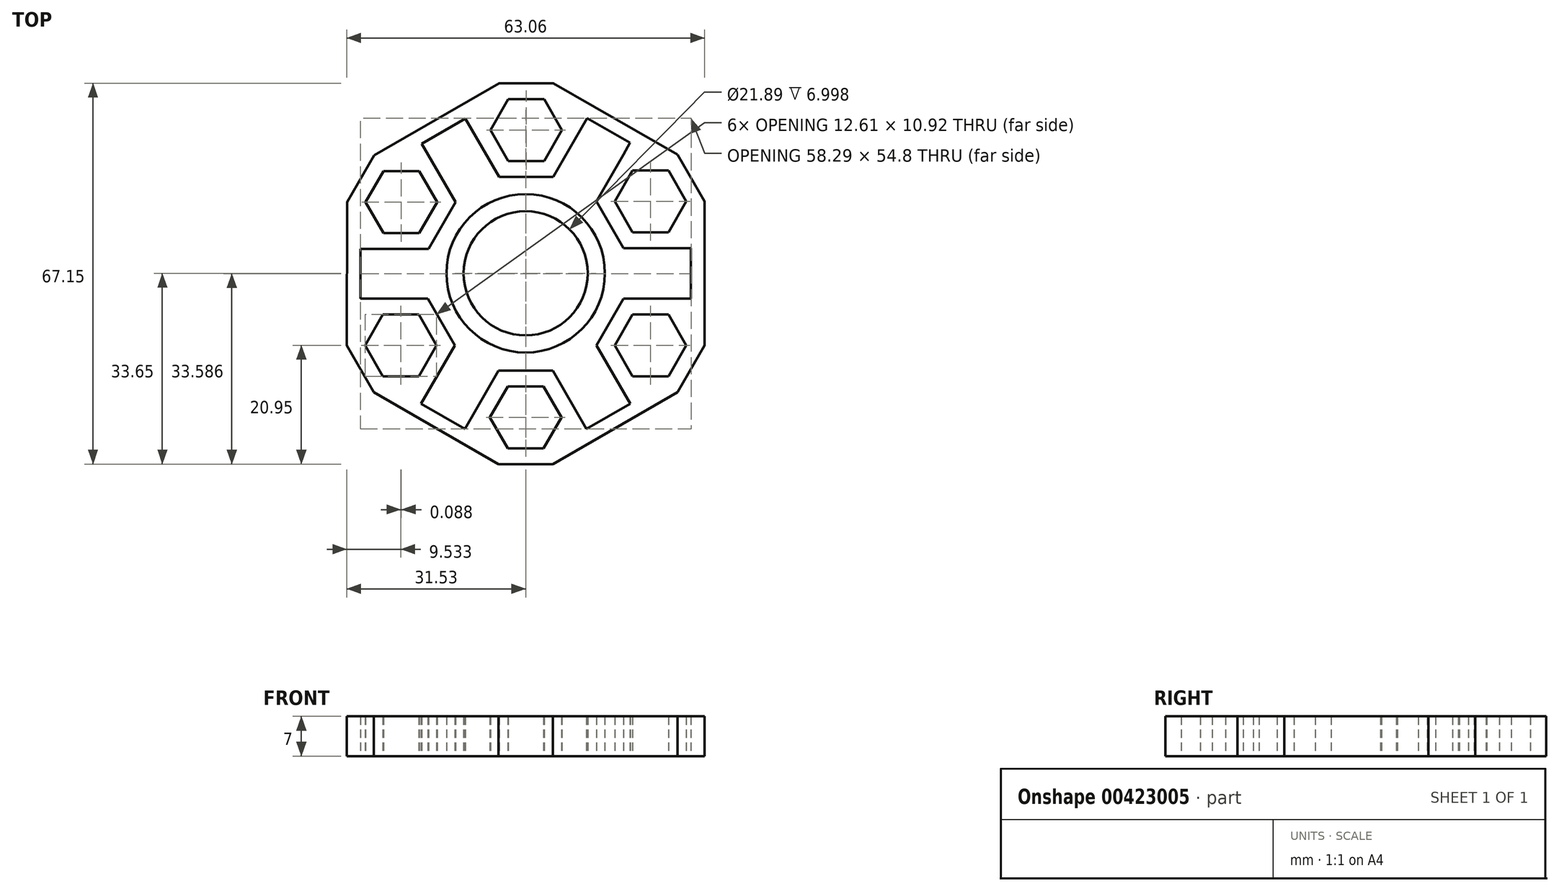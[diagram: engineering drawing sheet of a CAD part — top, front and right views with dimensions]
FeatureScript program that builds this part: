
annotation { "Feature Type Name" : "Feature", "Feature Type Description" : "" }
export const myFeature = defineFeature(function(context is Context, id is Id, definition is map)
    precondition{}
    {
        {
            var Q0;
            Q0=qCreatedBy(makeId("Top.planeOp"),FACE);
            var sketch = newSketch(context, id + "F0", { "sketchPlane" : qUnion([Q0])});
            skCircle(sketch, "E0", {"center": v(0, 0) * mm, "radius": 10.95 * mm});
            skCircle(sketch, "E1.cCircle", {"center": v(0, 0) * mm, "radius": 14.29 * mm, "construction": true});
            skPoint(sketch, "E1.0.midPoint", {"position": v(0, 14.29) * mm});
            skPoint(sketch, "E2.endSnap0", {"position": v(0, -12.7) * mm});
            skCircle(sketch, "E3.cCircle", {"center": v(0.09, 25.25) * mm, "radius": 5.46 * mm, "construction": true});
            skLineSegment(sketch, "E3.0", {"start": v(3.24, 19.79) * mm, "end": v(-3.06, 19.79) * mm});
            skLineSegment(sketch, "E3.1", {"start": v(-3.06, 19.79) * mm, "end": v(-6.22, 25.25) * mm});
            skLineSegment(sketch, "E3.2", {"start": v(-6.22, 25.25) * mm, "end": v(-3.06, 30.7) * mm});
            skLineSegment(sketch, "E3.3", {"start": v(-3.06, 30.7) * mm, "end": v(3.24, 30.7) * mm});
            skLineSegment(sketch, "E3.4", {"start": v(3.24, 30.7) * mm, "end": v(6.4, 25.25) * mm});
            skLineSegment(sketch, "E3.5", {"start": v(6.4, 25.25) * mm, "end": v(3.24, 19.79) * mm});
            skPoint(sketch, "E3.0.midPoint", {"position": v(0.09, 19.79) * mm});
            skCircle(sketch, "E4.cCircle", {"center": v(22, 12.7) * mm, "radius": 5.46 * mm, "construction": true});
            skLineSegment(sketch, "E4.0", {"start": v(18.84, 7.24) * mm, "end": v(15.7, 12.7) * mm});
            skLineSegment(sketch, "E4.1", {"start": v(15.7, 12.7) * mm, "end": v(18.84, 18.16) * mm});
            skLineSegment(sketch, "E4.2", {"start": v(18.84, 18.16) * mm, "end": v(25.15, 18.16) * mm});
            skLineSegment(sketch, "E4.3", {"start": v(25.15, 18.16) * mm, "end": v(28.3, 12.7) * mm});
            skLineSegment(sketch, "E4.4", {"start": v(28.3, 12.7) * mm, "end": v(25.15, 7.24) * mm});
            skLineSegment(sketch, "E4.5", {"start": v(25.15, 7.24) * mm, "end": v(18.84, 7.24) * mm});
            skPoint(sketch, "E4.0.midPoint", {"position": v(17.27, 9.97) * mm});
            skCircle(sketch, "E5.cCircle", {"center": v(22, -12.7) * mm, "radius": 5.46 * mm, "construction": true});
            skLineSegment(sketch, "E5.0", {"start": v(15.7, -12.7) * mm, "end": v(18.84, -7.24) * mm});
            skLineSegment(sketch, "E5.1", {"start": v(18.84, -7.24) * mm, "end": v(25.15, -7.24) * mm});
            skLineSegment(sketch, "E5.2", {"start": v(25.15, -7.24) * mm, "end": v(28.3, -12.7) * mm});
            skLineSegment(sketch, "E5.3", {"start": v(28.3, -12.7) * mm, "end": v(25.15, -18.16) * mm});
            skLineSegment(sketch, "E5.4", {"start": v(25.15, -18.16) * mm, "end": v(18.84, -18.16) * mm});
            skLineSegment(sketch, "E5.5", {"start": v(18.84, -18.16) * mm, "end": v(15.7, -12.7) * mm});
            skPoint(sketch, "E5.0.midPoint", {"position": v(17.27, -9.97) * mm});
            skCircle(sketch, "E6.cCircle", {"center": v(0, -25.4) * mm, "radius": 5.46 * mm, "construction": true});
            skLineSegment(sketch, "E6.0", {"start": v(-3.15, -19.94) * mm, "end": v(3.15, -19.94) * mm});
            skLineSegment(sketch, "E6.1", {"start": v(3.15, -19.94) * mm, "end": v(6.3, -25.4) * mm});
            skLineSegment(sketch, "E6.2", {"start": v(6.3, -25.4) * mm, "end": v(3.15, -30.86) * mm});
            skLineSegment(sketch, "E6.3", {"start": v(3.15, -30.86) * mm, "end": v(-3.15, -30.86) * mm});
            skLineSegment(sketch, "E6.4", {"start": v(-3.15, -30.86) * mm, "end": v(-6.3, -25.4) * mm});
            skLineSegment(sketch, "E6.5", {"start": v(-6.3, -25.4) * mm, "end": v(-3.15, -19.94) * mm});
            skPoint(sketch, "E6.0.midPoint", {"position": v(0, -19.94) * mm});
            skCircle(sketch, "E7.cCircle", {"center": v(-22, -12.7) * mm, "radius": 5.46 * mm, "construction": true});
            skLineSegment(sketch, "E7.0", {"start": v(-18.84, -7.24) * mm, "end": v(-15.7, -12.7) * mm});
            skLineSegment(sketch, "E7.1", {"start": v(-15.7, -12.7) * mm, "end": v(-18.84, -18.16) * mm});
            skLineSegment(sketch, "E7.2", {"start": v(-18.84, -18.16) * mm, "end": v(-25.15, -18.16) * mm});
            skLineSegment(sketch, "E7.3", {"start": v(-25.15, -18.16) * mm, "end": v(-28.3, -12.7) * mm});
            skLineSegment(sketch, "E7.4", {"start": v(-28.3, -12.7) * mm, "end": v(-25.15, -7.24) * mm});
            skLineSegment(sketch, "E7.5", {"start": v(-25.15, -7.24) * mm, "end": v(-18.84, -7.24) * mm});
            skPoint(sketch, "E7.0.midPoint", {"position": v(-17.27, -9.97) * mm});
            skCircle(sketch, "E8.cCircle", {"center": v(-21.9, 12.55) * mm, "radius": 5.46 * mm, "construction": true});
            skLineSegment(sketch, "E8.0", {"start": v(-15.6, 12.55) * mm, "end": v(-18.76, 7.09) * mm});
            skLineSegment(sketch, "E8.1", {"start": v(-18.76, 7.09) * mm, "end": v(-25.06, 7.09) * mm});
            skLineSegment(sketch, "E8.2", {"start": v(-25.06, 7.09) * mm, "end": v(-28.21, 12.55) * mm});
            skLineSegment(sketch, "E8.3", {"start": v(-28.21, 12.55) * mm, "end": v(-25.06, 18) * mm});
            skLineSegment(sketch, "E8.4", {"start": v(-25.06, 18) * mm, "end": v(-18.76, 18) * mm});
            skLineSegment(sketch, "E8.5", {"start": v(-18.76, 18) * mm, "end": v(-15.6, 12.55) * mm});
            skPoint(sketch, "E8.0.midPoint", {"position": v(-17.18, 9.82) * mm});
            skCircle(sketch, "E9.cCircle", {"center": v(-21.9, 12.55) * mm, "radius": 8.26 * mm, "construction": true});
            skLineSegment(sketch, "E9.0", {"start": v(-12.38, 12.55) * mm, "end": v(-17.14, 4.3) * mm});
            skLineSegment(sketch, "E9.1", {"start": v(-17.14, 4.3) * mm, "end": v(-26.67, 4.3) * mm});
            skLineSegment(sketch, "E9.2", {"start": v(-26.67, 4.3) * mm, "end": v(-31.44, 12.55) * mm});
            skLineSegment(sketch, "E9.3", {"start": v(-31.44, 12.55) * mm, "end": v(-26.67, 20.8) * mm});
            skLineSegment(sketch, "E9.4", {"start": v(-26.67, 20.8) * mm, "end": v(-17.14, 20.8) * mm});
            skLineSegment(sketch, "E9.5", {"start": v(-17.14, 20.8) * mm, "end": v(-12.38, 12.55) * mm});
            skPoint(sketch, "E9.0.midPoint", {"position": v(-14.76, 8.42) * mm});
            skCircle(sketch, "E10.cCircle", {"center": v(0.09, 25.25) * mm, "radius": 8.26 * mm, "construction": true});
            skLineSegment(sketch, "E10.0", {"start": v(4.85, 17) * mm, "end": v(-4.68, 17) * mm});
            skLineSegment(sketch, "E10.1", {"start": v(-4.68, 17) * mm, "end": v(-9.44, 25.25) * mm});
            skLineSegment(sketch, "E10.2", {"start": v(-9.44, 25.25) * mm, "end": v(-4.68, 33.5) * mm});
            skLineSegment(sketch, "E10.3", {"start": v(-4.68, 33.5) * mm, "end": v(4.85, 33.5) * mm});
            skLineSegment(sketch, "E10.4", {"start": v(4.85, 33.5) * mm, "end": v(9.62, 25.25) * mm});
            skLineSegment(sketch, "E10.5", {"start": v(9.62, 25.25) * mm, "end": v(4.85, 17) * mm});
            skPoint(sketch, "E10.0.midPoint", {"position": v(0.09, 17) * mm});
            skCircle(sketch, "E11.cCircle", {"center": v(22, 12.7) * mm, "radius": 8.26 * mm, "construction": true});
            skLineSegment(sketch, "E11.0", {"start": v(17.23, 4.45) * mm, "end": v(12.46, 12.7) * mm});
            skLineSegment(sketch, "E11.1", {"start": v(12.46, 12.7) * mm, "end": v(17.23, 20.96) * mm});
            skLineSegment(sketch, "E11.2", {"start": v(17.23, 20.96) * mm, "end": v(26.76, 20.96) * mm});
            skLineSegment(sketch, "E11.3", {"start": v(26.76, 20.96) * mm, "end": v(31.53, 12.7) * mm});
            skLineSegment(sketch, "E11.4", {"start": v(31.53, 12.7) * mm, "end": v(26.76, 4.45) * mm});
            skLineSegment(sketch, "E11.5", {"start": v(26.76, 4.45) * mm, "end": v(17.23, 4.45) * mm});
            skPoint(sketch, "E11.0.midPoint", {"position": v(14.85, 8.57) * mm});
            skCircle(sketch, "E12.cCircle", {"center": v(22, -12.7) * mm, "radius": 8.26 * mm, "construction": true});
            skLineSegment(sketch, "E12.0", {"start": v(12.46, -12.7) * mm, "end": v(17.23, -4.44) * mm});
            skLineSegment(sketch, "E12.1", {"start": v(17.23, -4.45) * mm, "end": v(26.76, -4.44) * mm});
            skLineSegment(sketch, "E12.2", {"start": v(26.76, -4.44) * mm, "end": v(31.53, -12.7) * mm});
            skLineSegment(sketch, "E12.3", {"start": v(31.53, -12.7) * mm, "end": v(26.76, -20.96) * mm});
            skLineSegment(sketch, "E12.4", {"start": v(26.76, -20.96) * mm, "end": v(17.23, -20.96) * mm});
            skLineSegment(sketch, "E12.5", {"start": v(17.23, -20.96) * mm, "end": v(12.46, -12.7) * mm});
            skPoint(sketch, "E12.0.midPoint", {"position": v(14.85, -8.57) * mm});
            skCircle(sketch, "E13.cCircle", {"center": v(0, -25.4) * mm, "radius": 8.26 * mm, "construction": true});
            skLineSegment(sketch, "E13.0", {"start": v(-4.77, -17.14) * mm, "end": v(4.77, -17.14) * mm});
            skLineSegment(sketch, "E13.1", {"start": v(4.77, -17.15) * mm, "end": v(9.53, -25.4) * mm});
            skLineSegment(sketch, "E13.2", {"start": v(9.53, -25.4) * mm, "end": v(4.77, -33.65) * mm});
            skLineSegment(sketch, "E13.3", {"start": v(4.77, -33.65) * mm, "end": v(-4.77, -33.66) * mm});
            skLineSegment(sketch, "E13.4", {"start": v(-4.77, -33.66) * mm, "end": v(-9.53, -25.4) * mm});
            skLineSegment(sketch, "E13.5", {"start": v(-9.53, -25.4) * mm, "end": v(-4.77, -17.15) * mm});
            skPoint(sketch, "E13.0.midPoint", {"position": v(0, -17.14) * mm});
            skCircle(sketch, "E14.cCircle", {"center": v(-22, -12.7) * mm, "radius": 8.26 * mm, "construction": true});
            skLineSegment(sketch, "E14.0", {"start": v(-17.23, -4.45) * mm, "end": v(-12.46, -12.7) * mm});
            skLineSegment(sketch, "E14.1", {"start": v(-12.46, -12.7) * mm, "end": v(-17.23, -20.96) * mm});
            skLineSegment(sketch, "E14.2", {"start": v(-17.23, -20.96) * mm, "end": v(-26.76, -20.96) * mm});
            skLineSegment(sketch, "E14.3", {"start": v(-26.76, -20.96) * mm, "end": v(-31.53, -12.7) * mm});
            skLineSegment(sketch, "E14.4", {"start": v(-31.53, -12.7) * mm, "end": v(-26.76, -4.45) * mm});
            skLineSegment(sketch, "E14.5", {"start": v(-26.76, -4.45) * mm, "end": v(-17.23, -4.45) * mm});
            skPoint(sketch, "E14.0.midPoint", {"position": v(-14.85, -8.57) * mm});
            skLineSegment(sketch, "E15", {"start": v(-14.21, 15.73) * mm, "end": v(-15.4, 17.77) * mm});
            skLineSegment(sketch, "E16", {"start": v(-23.27, -4.45) * mm, "end": v(-20.73, -4.45) * mm});
            skLineSegment(sketch, "E17", {"start": v(-7.78, -22.37) * mm, "end": v(-6.51, -20.17) * mm});
            skLineSegment(sketch, "E18", {"start": v(14.21, -15.73) * mm, "end": v(15.48, -17.93) * mm});
            skLineSegment(sketch, "E19", {"start": v(20.73, 4.45) * mm, "end": v(23.27, 4.45) * mm});
            skLineSegment(sketch, "E20", {"start": v(6.65, 20.1) * mm, "end": v(7.92, 22.3) * mm});
            skLineSegment(sketch, "E21.top", {"start": v(-1.27, -17.14) * mm, "end": v(1.27, -17.14) * mm});
            skLineSegment(sketch, "E22.bottom", {"start": v(1.27, 12.7) * mm, "end": v(-1.27, 12.7) * mm});
            skLineSegment(sketch, "E22.top", {"start": v(1.27, 17) * mm, "end": v(-1.27, 17) * mm});
            skLineSegment(sketch, "E23", {"start": v(11.6, 8.35) * mm, "end": v(12.73, 5.75) * mm});
            skLineSegment(sketch, "E24", {"start": v(13.03, -5.87) * mm, "end": v(11.81, -8.1) * mm});
            skLineSegment(sketch, "E25", {"start": v(-14.21, -9.67) * mm, "end": v(-15.48, -7.47) * mm});
            skLineSegment(sketch, "E26", {"start": v(-15.35, 7.4) * mm, "end": v(-14.08, 9.6) * mm});
            skLineSegment(sketch, "E27", {"start": v(-11.63, 5.25) * mm, "end": v(-10.36, 7.45) * mm});
            skLineSegment(sketch, "E28", {"start": v(-14.08, 9.6) * mm, "end": v(-15.35, 7.4) * mm});
            skLineSegment(sketch, "E29", {"start": v(15.48, 7.47) * mm, "end": v(14.21, 9.67) * mm});
            skLineSegment(sketch, "E30", {"start": v(-15.48, -7.47) * mm, "end": v(-14.21, -9.67) * mm});
            skLineSegment(sketch, "E31", {"start": v(-10.36, -7.45) * mm, "end": v(-11.63, -5.25) * mm});
            skCircle(sketch, "E32", {"center": v(0, 0) * mm, "radius": 11.08 * mm});
            skLineSegment(sketch, "E33", {"start": v(-31.44, 12.55) * mm, "end": v(-31.53, -12.7) * mm});
            skLineSegment(sketch, "E34", {"start": v(-26.76, -20.96) * mm, "end": v(-4.77, -33.66) * mm});
            skLineSegment(sketch, "E35", {"start": v(4.77, -33.65) * mm, "end": v(26.76, -20.96) * mm});
            skLineSegment(sketch, "E36", {"start": v(31.53, -12.7) * mm, "end": v(31.53, 12.7) * mm});
            skLineSegment(sketch, "E37", {"start": v(26.76, 20.96) * mm, "end": v(4.85, 33.5) * mm});
            skLineSegment(sketch, "E38", {"start": v(-4.68, 33.5) * mm, "end": v(-26.67, 20.8) * mm});
            skLineSegment(sketch, "E39", {"start": v(-21.9, 20.8) * mm, "end": v(-7.06, 29.37) * mm});
            skLineSegment(sketch, "E40", {"start": v(7.24, 29.37) * mm, "end": v(22, 20.96) * mm});
            skLineSegment(sketch, "E41", {"start": v(29.15, 8.57) * mm, "end": v(29.15, -8.57) * mm});
            skLineSegment(sketch, "E42", {"start": v(22, -20.96) * mm, "end": v(7.15, -29.53) * mm});
            skLineSegment(sketch, "E43", {"start": v(-7.15, -29.53) * mm, "end": v(-22, -20.96) * mm});
            skLineSegment(sketch, "E44", {"start": v(-29.15, -8.57) * mm, "end": v(-29.15, 8.57) * mm});
            skCircle(sketch, "E45", {"center": v(0, 0) * mm, "radius": 13.97 * mm});
            skLineSegment(sketch, "E46", {"start": v(-17.23, -4.45) * mm, "end": v(-13.76, -2.44) * mm});
            skLineSegment(sketch, "E47", {"start": v(-12.46, -12.7) * mm, "end": v(-8.99, -10.7) * mm});
            skLineSegment(sketch, "E48", {"start": v(17.23, 4.45) * mm, "end": v(13.76, 2.44) * mm});
            skLineSegment(sketch, "E49", {"start": v(12.46, 12.7) * mm, "end": v(8.99, 10.7) * mm});
            skLineSegment(sketch, "E50", {"start": v(-9.44, 25.25) * mm, "end": v(-10.64, 27.31) * mm});
            skLineSegment(sketch, "E51", {"start": v(-17.14, 20.8) * mm, "end": v(-18.33, 22.87) * mm});
            skLineSegment(sketch, "E52", {"start": v(9.62, 25.25) * mm, "end": v(10.81, 27.34) * mm});
            skLineSegment(sketch, "E53", {"start": v(17.23, 20.96) * mm, "end": v(18.4, 23) * mm});
            skLineSegment(sketch, "E54", {"start": v(26.76, 4.45) * mm, "end": v(29.15, 4.45) * mm});
            skLineSegment(sketch, "E55", {"start": v(26.76, -4.44) * mm, "end": v(29.15, -4.44) * mm});
            skLineSegment(sketch, "E56", {"start": v(17.23, -20.96) * mm, "end": v(18.42, -23.02) * mm});
            skLineSegment(sketch, "E57", {"start": v(9.53, -25.4) * mm, "end": v(10.72, -27.46) * mm});
            skLineSegment(sketch, "E58", {"start": v(-9.53, -25.4) * mm, "end": v(-10.72, -27.46) * mm});
            skLineSegment(sketch, "E59", {"start": v(-17.23, -20.96) * mm, "end": v(-18.42, -23.02) * mm});
            skLineSegment(sketch, "E60", {"start": v(-26.76, -4.45) * mm, "end": v(-29.15, -4.45) * mm});
            skLineSegment(sketch, "E61", {"start": v(-26.67, 4.3) * mm, "end": v(-29.15, 4.3) * mm});
            skSolve(sketch);
        }
        {
            var Q0;
            Q0=qSketchRegion(id+"F0",true);
            var Q1;
            Q1=makeQuery(id+"F0.imprint","IMPRINT",FACE,{"disambiguationData":[TD([[makeQuery(id+"F0.imprint","IMPRINT",EDGE,{"derivedFrom":sQuery(id+"F0.wireOp",EDGE,"E22.bottom")}),-1.0]])]});
            var Q2;
            Q2=makeQuery(id+"F0.imprint","IMPRINT",FACE,{"disambiguationData":[TD([[makeQuery(id+"F0.imprint","IMPRINT",EDGE,{"derivedFrom":sQuery(id+"F0.wireOp",EDGE,"r9I69o4T-baSL-ddfZ-GocF-frNLYwVvmABk")}),1.0]])]});
            var Q3;
            Q3=makeQuery(id+"F0.imprint","IMPRINT",FACE,{"disambiguationData":[TD([[makeQuery(id+"F0.imprint","IMPRINT",EDGE,{"derivedFrom":sQuery(id+"F0.wireOp",EDGE,"E21.bottom")}),-1.0]])]});
            var Q4;
            {var subQ0=sQuery(id+"F0.wireOp",EDGE,"6sW6mJ2L-ygAF-Vdi4-I9HX-WlLPKnymDywZ");Q4=makeQuery(id+"F0.imprint","IMPRINT",FACE,{"disambiguationData":[TD([[makeQuery(id+"F0.imprint","IMPRINT",EDGE,{"derivedFrom":subQ0}),1.0]])]});}
            var Q5;
            {var subQ0=sQuery(id+"F0.wireOp",EDGE,"8BQQ6vlK-IiWs-5aLy-QiVH-YKUD170Bbk5W");Q5=makeQuery(id+"F0.imprint","IMPRINT",FACE,{"disambiguationData":[TD([[makeQuery(id+"F0.imprint","IMPRINT",EDGE,{"derivedFrom":subQ0}),1.0]])]});}
            var Q6;
            Q6=makeQuery(id+"F0.imprint","IMPRINT",FACE,{"disambiguationData":[TD([[makeQuery(id+"F0.imprint","IMPRINT",EDGE,{"derivedFrom":sQuery(id+"F0.wireOp",EDGE,"WzqIBDOR-9Q7D-lWyq-SiJA-YPrxWTZHhMYv")}),-1.0]])]});
            var Q7;
            {var subQ4=sQuery(id+"F0.wireOp",EDGE,"E30");Q7=makeQuery(id+"F0.imprint","IMPRINT",FACE,{"disambiguationData":[TD([[makeQuery(id+"F0.imprint","IMPRINT",EDGE,{"derivedFrom":subQ4}),1.0]])]});}
            var Q8;
            {var subQ4=sQuery(id+"F0.wireOp",EDGE,"E29");Q8=makeQuery(id+"F0.imprint","IMPRINT",FACE,{"disambiguationData":[TD([[makeQuery(id+"F0.imprint","IMPRINT",EDGE,{"derivedFrom":subQ4}),1.0]])]});}
            var Q9;
            {var subQ0=sQuery(id+"F0.wireOp",EDGE,"E51");Q9=makeQuery(id+"F0.imprint","IMPRINT",FACE,{"disambiguationData":[TD([[makeQuery(id+"F0.imprint","IMPRINT",EDGE,{"derivedFrom":subQ0}),1.0]])]});}
            var Q10;
            {var subQ0=sQuery(id+"F0.wireOp",EDGE,"E50");Q10=makeQuery(id+"F0.imprint","IMPRINT",FACE,{"disambiguationData":[TD([[makeQuery(id+"F0.imprint","IMPRINT",EDGE,{"derivedFrom":subQ0}),-1.0]])]});}
            var Q11;
            {var subQ0=sQuery(id+"F0.wireOp",EDGE,"E52");Q11=makeQuery(id+"F0.imprint","IMPRINT",FACE,{"disambiguationData":[TD([[makeQuery(id+"F0.imprint","IMPRINT",EDGE,{"derivedFrom":subQ0}),1.0]])]});}
            var Q12;
            {var subQ0=sQuery(id+"F0.wireOp",EDGE,"E53");Q12=makeQuery(id+"F0.imprint","IMPRINT",FACE,{"disambiguationData":[TD([[makeQuery(id+"F0.imprint","IMPRINT",EDGE,{"derivedFrom":subQ0}),-1.0]])]});}
            var Q13;
            {var subQ0=sQuery(id+"F0.wireOp",EDGE,"E54");Q13=makeQuery(id+"F0.imprint","IMPRINT",FACE,{"disambiguationData":[TD([[makeQuery(id+"F0.imprint","IMPRINT",EDGE,{"derivedFrom":subQ0}),1.0]])]});}
            var Q14;
            {var subQ0=sQuery(id+"F0.wireOp",EDGE,"E55");Q14=makeQuery(id+"F0.imprint","IMPRINT",FACE,{"disambiguationData":[TD([[makeQuery(id+"F0.imprint","IMPRINT",EDGE,{"derivedFrom":subQ0}),-1.0]])]});}
            var Q15;
            {var subQ0=sQuery(id+"F0.wireOp",EDGE,"E56");Q15=makeQuery(id+"F0.imprint","IMPRINT",FACE,{"disambiguationData":[TD([[makeQuery(id+"F0.imprint","IMPRINT",EDGE,{"derivedFrom":subQ0}),1.0]])]});}
            var Q16;
            {var subQ0=sQuery(id+"F0.wireOp",EDGE,"E57");Q16=makeQuery(id+"F0.imprint","IMPRINT",FACE,{"disambiguationData":[TD([[makeQuery(id+"F0.imprint","IMPRINT",EDGE,{"derivedFrom":subQ0}),-1.0]])]});}
            var Q17;
            {var subQ0=sQuery(id+"F0.wireOp",EDGE,"E58");Q17=makeQuery(id+"F0.imprint","IMPRINT",FACE,{"disambiguationData":[TD([[makeQuery(id+"F0.imprint","IMPRINT",EDGE,{"derivedFrom":subQ0}),1.0]])]});}
            var Q18;
            {var subQ0=sQuery(id+"F0.wireOp",EDGE,"E59");Q18=makeQuery(id+"F0.imprint","IMPRINT",FACE,{"disambiguationData":[TD([[makeQuery(id+"F0.imprint","IMPRINT",EDGE,{"derivedFrom":subQ0}),-1.0]])]});}
            var Q19;
            {var subQ0=sQuery(id+"F0.wireOp",EDGE,"E60");Q19=makeQuery(id+"F0.imprint","IMPRINT",FACE,{"disambiguationData":[TD([[makeQuery(id+"F0.imprint","IMPRINT",EDGE,{"derivedFrom":subQ0}),1.0]])]});}
            var Q20;
            {var subQ0=sQuery(id+"F0.wireOp",EDGE,"E61");Q20=makeQuery(id+"F0.imprint","IMPRINT",FACE,{"disambiguationData":[TD([[makeQuery(id+"F0.imprint","IMPRINT",EDGE,{"derivedFrom":subQ0}),-1.0]])]});}
            var Q21;
            Q21=makeQuery(id+"F0.imprint","IMPRINT",FACE,{"disambiguationData":[TD([[makeQuery(id+"F0.imprint","IMPRINT",EDGE,{"derivedFrom":sQuery(id+"F0.wireOp",EDGE,"E0")}),-1.0]])]});
            var Q22;
            Q22=makeQuery(id+"F0.imprint","IMPRINT",FACE,{"disambiguationData":[TD([[makeQuery(id+"F0.imprint","IMPRINT",EDGE,{"derivedFrom":sQuery(id+"F0.wireOp",EDGE,"E32")}),-1.0]])]});
            extrude(context, id + "F1", {"entities" : qUnion([Q0, Q1, Q2, Q3, Q4, Q5, Q6, Q7, Q8, Q9, Q10, Q11, Q12, Q13, Q14, Q15, Q16, Q17, Q18, Q19, Q20, Q21, Q22]), "depth" : 7 * mm, "offsetDistance" : 25.4 * mm});
        }
        {
            var Q0;
            Q0=qCreatedBy(makeId("Top.planeOp"),FACE);
            var sketch = newSketch(context, id + "F2", { "sketchPlane" : qUnion([Q0])});
            skCircle(sketch, "E62", {"center": v(0, 0) * mm, "radius": 11.18 * mm});
            skCircle(sketch, "E63.cCircle", {"center": v(0, 0) * mm, "radius": 13.34 * mm, "construction": true});
            skPoint(sketch, "E63.0.midPoint", {"position": v(0, 13.33) * mm});
            skCircle(sketch, "E64", {"center": v(0, 0) * mm, "radius": 13.29 * mm});
            skSolve(sketch);
        }
        {
            var Q0;
            Q0=qSketchRegion(id+"F2",true);
            extrude(context, id + "F3", {"entities" : qUnion([Q0]), "operationType" : NewBodyOperationType.ADD, "depth" : 7 * mm});
        }
    });
